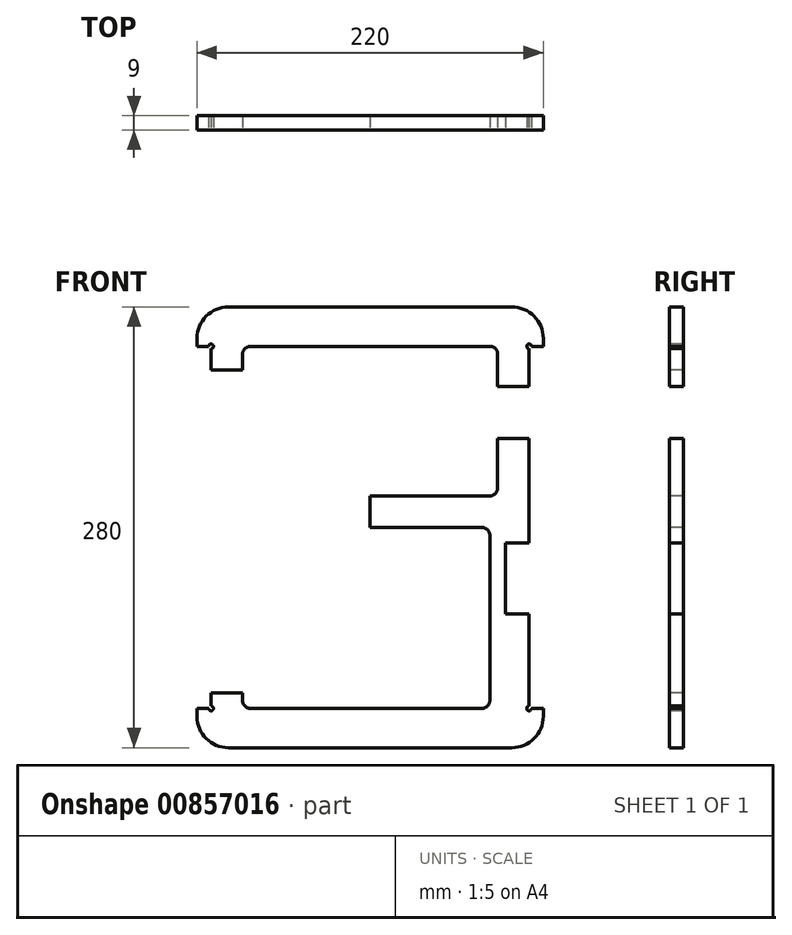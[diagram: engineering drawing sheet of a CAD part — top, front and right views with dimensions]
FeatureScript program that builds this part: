
annotation { "Feature Type Name" : "Feature", "Feature Type Description" : "" }
export const myFeature = defineFeature(function(context is Context, id is Id, definition is map)
    precondition{}
    {
        {
            var Q0;
            Q0=qCreatedBy(makeId("Front.planeOp"),FACE);
            var sketch = newSketch(context, id + "F0", { "sketchPlane" : qUnion([Q0])});
            skLineSegment(sketch, "E0.bottom", {"start": v(-99.41, 134.79) * mm, "end": v(80.59, 134.79) * mm});
            skLineSegment(sketch, "E0.top", {"start": v(-99.41, -145.21) * mm, "end": v(80.59, -145.21) * mm});
            skLineSegment(sketch, "E0.left", {"start": v(-119.41, 114.79) * mm, "end": v(-119.41, 109.79) * mm});
            skLineSegment(sketch, "E0.right", {"start": v(100.59, 114.79) * mm, "end": v(100.59, 109.79) * mm});
            skPoint(sketch, "E0.middle", {"position": v(-9.41, -5.21) * mm});
            skLineSegment(sketch, "E1.bottom", {"start": v(-9.41, 14.79) * mm, "end": v(66.59, 14.79) * mm});
            skLineSegment(sketch, "E2", {"start": v(-119.41, 109.79) * mm, "end": v(-110.41, 109.79) * mm});
            skLineSegment(sketch, "E3", {"start": v(-119.41, -120.21) * mm, "end": v(-110.41, -120.21) * mm});
            skLineSegment(sketch, "E4.0", {"start": v(-110.41, 109.79) * mm, "end": v(-110.41, 94.79) * mm});
            skLineSegment(sketch, "E5.trimOffspring", {"start": v(-119.41, -120.21) * mm, "end": v(-119.41, -125.21) * mm});
            skLineSegment(sketch, "E6.0", {"start": v(-90.41, 104.79) * mm, "end": v(-90.41, 94.79) * mm});
            skLineSegment(sketch, "E7.0", {"start": v(71.59, 104.79) * mm, "end": v(71.59, 84.29) * mm});
            skLineSegment(sketch, "E8.trimOffspring", {"start": v(-85.41, 109.79) * mm, "end": v(66.59, 109.79) * mm});
            skLineSegment(sketch, "E9.trimOffspring", {"start": v(-85.41, -120.21) * mm, "end": v(61.59, -120.21) * mm});
            skLineSegment(sketch, "E10.trimOffspring", {"start": v(-9.41, -5.21) * mm, "end": v(61.59, -5.21) * mm});
            skPoint(sketch, "E11.visualSharp", {"position": v(-119.41, 134.79) * mm});
            skArc(sketch, "E11.filletArc", {"start": v(-99.41, 134.79) * mm, "mid": v(-113.55, 128.93) * mm, "end": v(-119.41, 114.79) * mm});
            skPoint(sketch, "E12.visualSharp", {"position": v(100.59, 134.79) * mm});
            skArc(sketch, "E12.filletArc", {"start": v(100.59, 114.79) * mm, "mid": v(94.73, 128.93) * mm, "end": v(80.59, 134.79) * mm});
            skPoint(sketch, "E13.visualSharp", {"position": v(100.59, -145.21) * mm});
            skArc(sketch, "E13.filletArc", {"start": v(80.59, -145.21) * mm, "mid": v(94.73, -139.35) * mm, "end": v(100.59, -125.21) * mm});
            skPoint(sketch, "E14.visualSharp", {"position": v(-119.41, -145.21) * mm});
            skArc(sketch, "E14.filletArc", {"start": v(-119.41, -125.21) * mm, "mid": v(-113.55, -139.35) * mm, "end": v(-99.41, -145.21) * mm});
            skLineSegment(sketch, "E15.trimOffspring", {"start": v(100.59, -120.21) * mm, "end": v(100.59, -125.21) * mm});
            skLineSegment(sketch, "E16.trimOffspring", {"start": v(91.59, -120.21) * mm, "end": v(100.59, -120.21) * mm});
            skLineSegment(sketch, "E17.trimOffspring", {"start": v(91.59, 109.79) * mm, "end": v(91.59, 84.29) * mm});
            skLineSegment(sketch, "E18.trimOffspring", {"start": v(91.59, 109.79) * mm, "end": v(100.59, 109.79) * mm});
            skPoint(sketch, "E19.visualSharp", {"position": v(71.59, 14.79) * mm});
            skArc(sketch, "E19.filletArc", {"start": v(66.59, 14.79) * mm, "mid": v(70.13, 16.25) * mm, "end": v(71.59, 19.79) * mm});
            skPoint(sketch, "E20.visualSharp", {"position": v(-90.41, 14.79) * mm});
            skPoint(sketch, "E21.visualSharp", {"position": v(-90.41, -5.21) * mm});
            skPoint(sketch, "E22.visualSharp", {"position": v(-90.41, -120.21) * mm});
            skArc(sketch, "E22.filletArc", {"start": v(-90.41, -115.21) * mm, "mid": v(-88.95, -118.75) * mm, "end": v(-85.41, -120.21) * mm});
            skPoint(sketch, "E23.visualSharp", {"position": v(-90.41, 109.79) * mm});
            skArc(sketch, "E23.filletArc", {"start": v(-85.41, 109.79) * mm, "mid": v(-88.95, 108.32) * mm, "end": v(-90.41, 104.79) * mm});
            skPoint(sketch, "E24.visualSharp", {"position": v(71.59, 109.79) * mm});
            skArc(sketch, "E24.filletArc", {"start": v(71.59, 104.79) * mm, "mid": v(70.13, 108.32) * mm, "end": v(66.59, 109.79) * mm});
            skCircle(sketch, "E25", {"center": v(-110.41, 109.79) * mm, "radius": 1.5 * mm});
            skCircle(sketch, "E26", {"center": v(91.59, 109.79) * mm, "radius": 1.5 * mm});
            skCircle(sketch, "E27", {"center": v(-110.41, -120.21) * mm, "radius": 1.5 * mm});
            skCircle(sketch, "E28", {"center": v(91.59, -120.21) * mm, "radius": 1.5 * mm});
            skLineSegment(sketch, "E29.bottom", {"start": v(-110.41, 94.79) * mm, "end": v(-90.41, 94.79) * mm});
            skLineSegment(sketch, "E29.top", {"start": v(-110.41, -110.21) * mm, "end": v(-90.41, -110.21) * mm});
            skLineSegment(sketch, "E29.right", {"start": v(91.59, 51.29) * mm, "end": v(91.59, -15.21) * mm});
            skLineSegment(sketch, "E30.trimOffspring", {"start": v(-90.41, -110.21) * mm, "end": v(-90.41, -115.21) * mm});
            skLineSegment(sketch, "E31.trimOffspring", {"start": v(-110.41, -110.21) * mm, "end": v(-110.41, -120.21) * mm});
            skLineSegment(sketch, "E32.left", {"start": v(-85.41, -5.21) * mm, "end": v(-85.41, -5.38) * mm});
            skPoint(sketch, "E33", {"position": v(91.59, -60.21) * mm});
            skLineSegment(sketch, "E34", {"start": v(91.59, -60.21) * mm, "end": v(76.59, -60.21) * mm});
            skLineSegment(sketch, "E35", {"start": v(91.59, -15.21) * mm, "end": v(76.59, -15.21) * mm});
            skLineSegment(sketch, "E36", {"start": v(76.59, -60.21) * mm, "end": v(76.59, -15.21) * mm});
            skLineSegment(sketch, "E37.trimOffspring", {"start": v(91.59, -60.21) * mm, "end": v(91.59, -110.21) * mm});
            skLineSegment(sketch, "E38.trimOffspring", {"start": v(91.59, -60.21) * mm, "end": v(91.59, -120.21) * mm});
            skLineSegment(sketch, "E39", {"start": v(66.59, -10.21) * mm, "end": v(66.59, -35.87) * mm});
            skLineSegment(sketch, "E40", {"start": v(66.59, -35.87) * mm, "end": v(66.59, -115.21) * mm});
            skPoint(sketch, "E41.visualSharp", {"position": v(66.59, -5.21) * mm});
            skArc(sketch, "E41.filletArc", {"start": v(66.59, -10.21) * mm, "mid": v(65.13, -6.68) * mm, "end": v(61.59, -5.21) * mm});
            skPoint(sketch, "E42.visualSharp", {"position": v(66.59, -120.21) * mm});
            skArc(sketch, "E42.filletArc", {"start": v(61.59, -120.21) * mm, "mid": v(65.13, -118.75) * mm, "end": v(66.59, -115.21) * mm});
            skPoint(sketch, "E43", {"position": v(56.25, 84.29) * mm});
            skPoint(sketch, "E44", {"position": v(61.33, 51.29) * mm});
            skLineSegment(sketch, "E45", {"start": v(71.59, 84.29) * mm, "end": v(91.59, 84.29) * mm});
            skLineSegment(sketch, "E46", {"start": v(71.59, 51.29) * mm, "end": v(91.59, 51.29) * mm});
            skLineSegment(sketch, "E47.trimOffspring", {"start": v(71.59, 51.29) * mm, "end": v(71.59, 19.79) * mm});
            skPoint(sketch, "E48.orphan", {"position": v(91.59, 79.79) * mm});
            skLineSegment(sketch, "E49", {"start": v(-9.41, -5.21) * mm, "end": v(-9.41, 14.79) * mm});
            skPoint(sketch, "E32.bottom.start.orphan", {"position": v(-85.41, 14.79) * mm});
            skSolve(sketch);
        }
        {
            var Q0;
            Q0=makeQuery(id+"F0.imprint","IMPRINT",FACE,{"disambiguationData":[TD([[makeQuery(id+"F0.imprint","IMPRINT",EDGE,{"derivedFrom":sQuery(id+"F0.wireOp",EDGE,"E0.bottom")}),-1.0]])]});
            var Q1;
            Q1=makeQuery(id+"F0.imprint","IMPRINT",FACE,{"disambiguationData":[TD([[makeQuery(id+"F0.imprint","IMPRINT",EDGE,{"derivedFrom":sQuery(id+"F0.wireOp",EDGE,"E0.top")}),1.0]])]});
            extrude(context, id + "F1", {"entities" : qUnion([Q0, Q1]), "oppositeDirection" : true, "depth" : 9 * mm, "offsetDistance" : 25 * mm});
        }
    });
